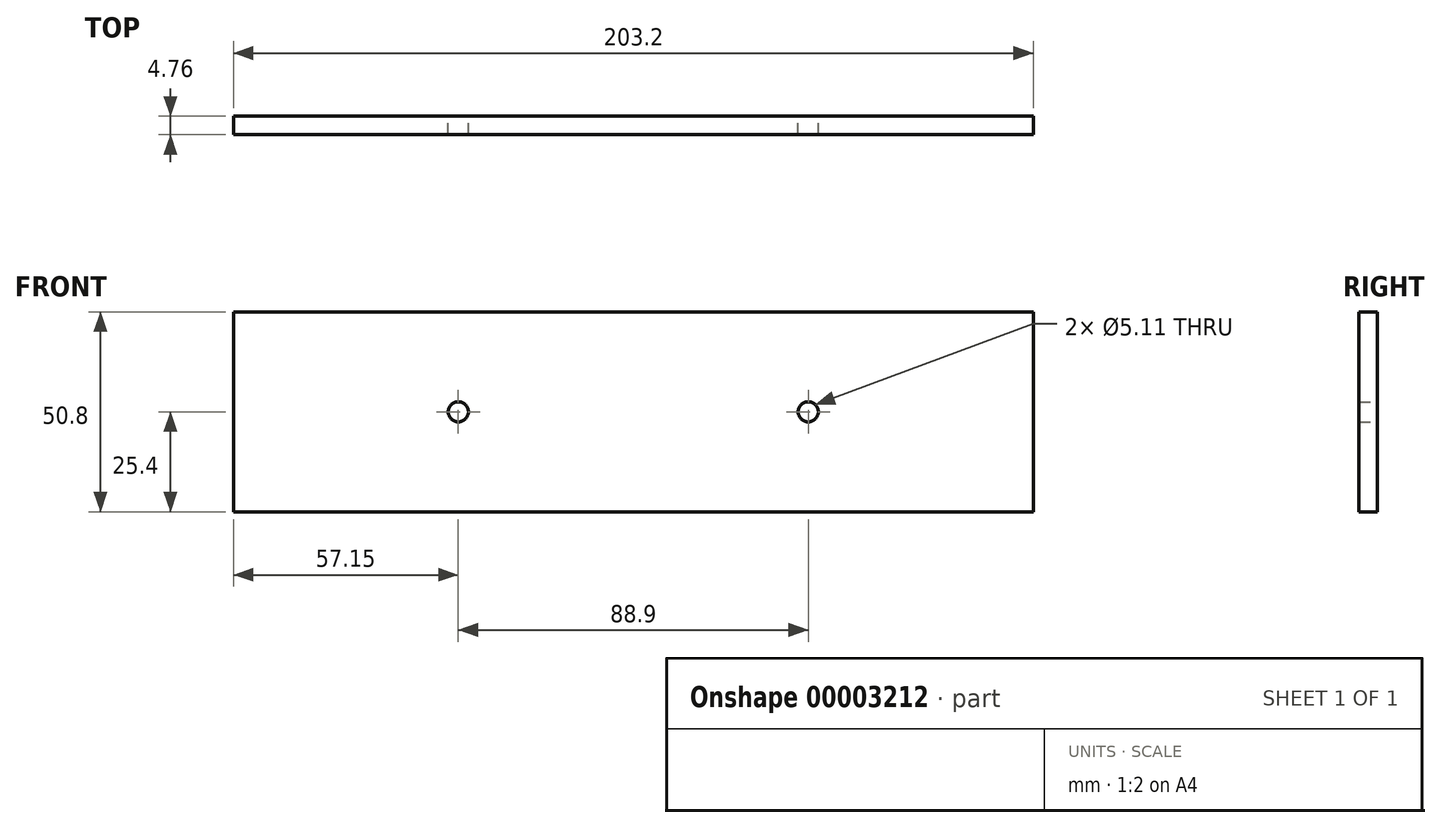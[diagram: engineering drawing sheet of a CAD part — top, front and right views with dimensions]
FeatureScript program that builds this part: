
annotation { "Feature Type Name" : "Feature", "Feature Type Description" : "" }
export const myFeature = defineFeature(function(context is Context, id is Id, definition is map)
    precondition{}
    {
        {
            var Q0;
            Q0=qCreatedBy(makeId("Front.planeOp"),FACE);
            var sketch = newSketch(context, id + "F0", { "sketchPlane" : qUnion([Q0])});
            skLineSegment(sketch, "E0", {"start": v(0, 0) * mm, "end": v(0, -50.8) * mm});
            skLineSegment(sketch, "E1", {"start": v(0, -50.8) * mm, "end": v(203.2, -50.8) * mm});
            skLineSegment(sketch, "E2", {"start": v(203.2, -50.8) * mm, "end": v(203.2, 0) * mm});
            skLineSegment(sketch, "E3", {"start": v(203.2, 0) * mm, "end": v(0, 0) * mm});
            skLineSegment(sketch, "E4", {"start": v(0, -25.4) * mm, "end": v(203.2, -25.4) * mm, "construction": true});
            skLineSegment(sketch, "E5", {"start": v(57.15, 0) * mm, "end": v(57.15, -50.8) * mm, "construction": true});
            skLineSegment(sketch, "E6", {"start": v(146.05, 0) * mm, "end": v(146.05, -50.8) * mm, "construction": true});
            skCircle(sketch, "E7", {"center": v(57.15, -25.4) * mm, "radius": 2.55 * mm});
            skCircle(sketch, "E8", {"center": v(146.05, -25.4) * mm, "radius": 2.55 * mm});
            skSolve(sketch);
        }
        {
            var Q0;
            Q0=makeQuery(id+"F0.imprint","IMPRINT",FACE,{"disambiguationData":[TD([[makeQuery(id+"F0.imprint","IMPRINT",EDGE,{"derivedFrom":sQuery(id+"F0.wireOp",EDGE,"E0")}),1.0]])]});
            extrude(context, id + "F1", {"entities" : qUnion([Q0]), "endBound" : BoundingType.SYMMETRIC, "depth" : 4.76 * mm});
        }
    });
